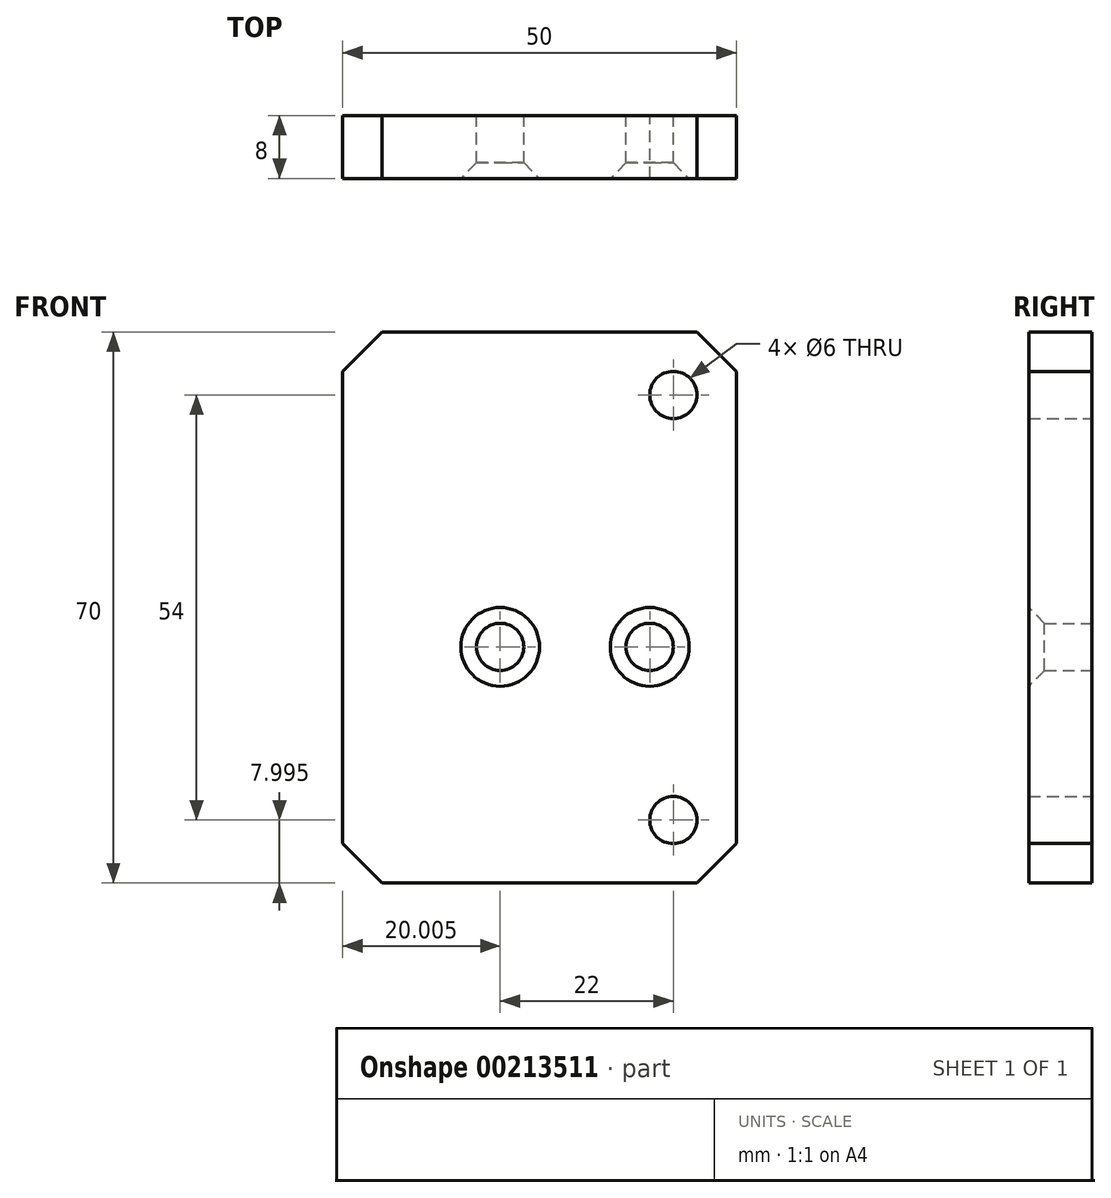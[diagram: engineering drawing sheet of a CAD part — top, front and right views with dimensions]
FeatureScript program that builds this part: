
annotation { "Feature Type Name" : "Feature", "Feature Type Description" : "" }
export const myFeature = defineFeature(function(context is Context, id is Id, definition is map)
    precondition{}
    {
        {
            var Q0;
            Q0=qCreatedBy(makeId("Front.planeOp"),FACE);
            var sketch = newSketch(context, id + "F0", { "sketchPlane" : qUnion([Q0])});
            skLineSegment(sketch, "E0.bottom", {"start": v(-30.02, 45) * mm, "end": v(19.98, 45) * mm});
            skLineSegment(sketch, "E0.top", {"start": v(-30.02, -25) * mm, "end": v(19.98, -25) * mm});
            skLineSegment(sketch, "E0.left", {"start": v(-30.02, 45) * mm, "end": v(-30.02, -25) * mm});
            skCircle(sketch, "E1", {"center": v(11.98, 37) * mm, "radius": 3 * mm});
            skLineSegment(sketch, "E2", {"start": v(-30.02, 10) * mm, "end": v(29.98, 10) * mm, "construction": true});
            skCircle(sketch, "E3.MirrorC", {"center": v(11.98, -17) * mm, "radius": 3 * mm});
            skCircle(sketch, "E4", {"center": v(-10.02, 5) * mm, "radius": 3 * mm});
            skCircle(sketch, "E5", {"center": v(8.98, 5) * mm, "radius": 3 * mm});
            skLineSegment(sketch, "E6", {"start": v(19.98, 45) * mm, "end": v(19.98, -25) * mm});
            skSolve(sketch);
        }
        {
            var Q0;
            Q0 = qSketchRegion(id + "F0", true);
            extrude(context, id + "F1", {"entities" : qUnion([Q0]), "depth" : 8 * mm});
        }
        {
            var Q0;
            Q0=makeQuery(id+"F1.opExtrude","CAP_EDGE",EDGE,{"disambiguationData":[OSD([sQuery(id+"F0.wireOp",EDGE,"E4")])],"isStart":false});
            var Q1;
            Q1=makeQuery(id+"F1.opExtrude","CAP_EDGE",EDGE,{"disambiguationData":[OSD([sQuery(id+"F0.wireOp",EDGE,"E5")])],"isStart":false});
            chamfer(context, id + "F2", {"entities" : qUnion([Q0, Q1]), "width" : 2 * mm, "tangentPropagation" : true});
        }
        {
            var Q0;
            Q0=makeQuery(id+"F1.opExtrude","SWEPT_EDGE",EDGE,{"disambiguationData":[OSD([sQuery(id+"F0.wireOp",EDGE,"E0.bottom"),sQuery(id+"F0.wireOp",EDGE,"E6")])]});
            var Q1;
            Q1=makeQuery(id+"F1.opExtrude","SWEPT_EDGE",EDGE,{"disambiguationData":[OSD([sQuery(id+"F0.wireOp",EDGE,"E0.top"),sQuery(id+"F0.wireOp",EDGE,"E6")])]});
            var Q2;
            Q2=makeQuery(id+"F1.opExtrude","SWEPT_EDGE",EDGE,{"disambiguationData":[OSD([sQuery(id+"F0.wireOp",EDGE,"E0.bottom"),sQuery(id+"F0.wireOp",EDGE,"E0.left")])]});
            var Q3;
            Q3=makeQuery(id+"F1.opExtrude","SWEPT_EDGE",EDGE,{"disambiguationData":[OSD([sQuery(id+"F0.wireOp",EDGE,"E0.top"),sQuery(id+"F0.wireOp",EDGE,"E0.left")])]});
            chamfer(context, id + "F3", {"entities" : qUnion([Q0, Q1, Q2, Q3]), "width" : 5 * mm, "tangentPropagation" : true});
        }
    });
